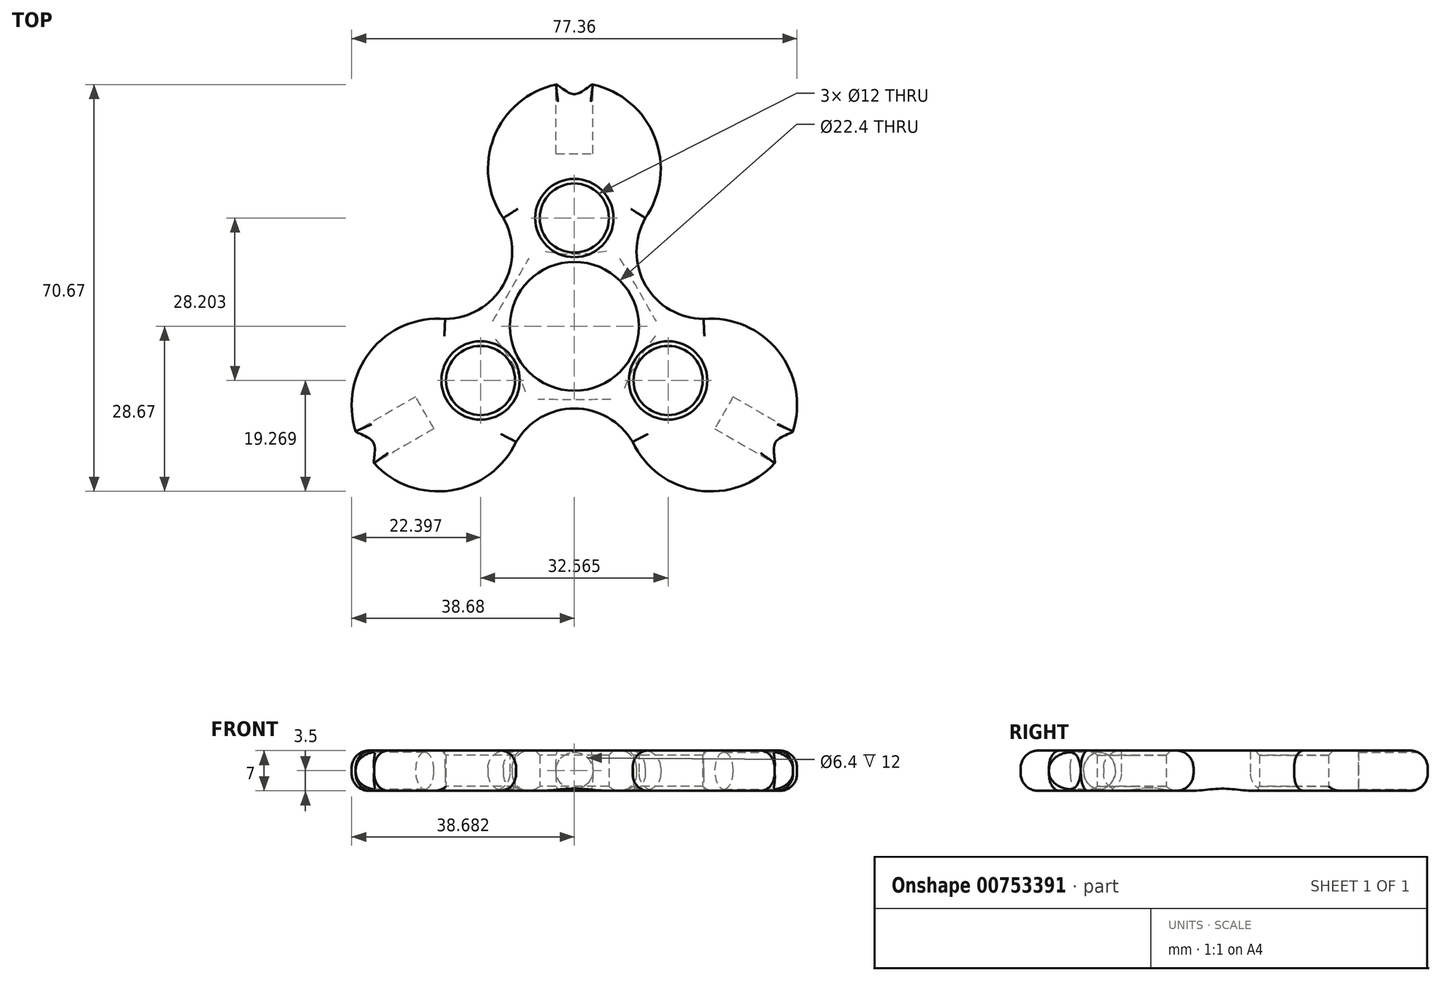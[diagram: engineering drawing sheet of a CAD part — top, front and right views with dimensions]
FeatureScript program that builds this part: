
annotation { "Feature Type Name" : "Feature", "Feature Type Description" : "" }
export const myFeature = defineFeature(function(context is Context, id is Id, definition is map)
    precondition{}
    {
        {
            var Q0;
            Q0=qCreatedBy(makeId("Top.planeOp"),FACE);
            var sketch = newSketch(context, id + "F0", { "sketchPlane" : qUnion([Q0])});
            skCircle(sketch, "E0", {"center": v(0, 0) * mm, "radius": 11.2 * mm});
            skLineSegment(sketch, "E1", {"start": v(0, 27.34) * mm, "end": v(0, -38.7) * mm, "construction": true});
            skArc(sketch, "E2", {"start": v(12.33, 18.8) * mm, "mid": v(13.96, 32.83) * mm, "end": v(3.2, 42) * mm});
            skPoint(sketch, "E3.startSnap0", {"position": v(0, 42.34) * mm});
            skArc(sketch, "E4", {"start": v(-3.2, 42) * mm, "mid": v(-13.96, 32.84) * mm, "end": v(-12.33, 18.8) * mm});
            skLineSegment(sketch, "E5", {"start": v(-3.2, 42) * mm, "end": v(-3.2, 42) * mm});
            skPoint(sketch, "E6.1.0", {"position": v(-36.67, -21.17) * mm});
            skArc(sketch, "E6.1.1", {"start": v(-34.77, -23.77) * mm, "mid": v(-21.46, -28.5) * mm, "end": v(-10.12, -20.08) * mm});
            skArc(sketch, "E6.1.3", {"start": v(-22.44, 1.28) * mm, "mid": v(-35.41, -4.33) * mm, "end": v(-37.97, -18.22) * mm});
            skPoint(sketch, "E6.2.0", {"position": v(36.67, -21.17) * mm});
            skArc(sketch, "E6.2.1", {"start": v(37.97, -18.23) * mm, "mid": v(35.42, -4.33) * mm, "end": v(22.45, 1.28) * mm});
            skArc(sketch, "E6.2.3", {"start": v(10.12, -20.07) * mm, "mid": v(21.45, -28.5) * mm, "end": v(34.77, -23.77) * mm});
            skArc(sketch, "E7", {"start": v(12.33, 18.8) * mm, "mid": v(12.37, 7.14) * mm, "end": v(22.45, 1.28) * mm});
            skArc(sketch, "E8.1.0", {"start": v(-22.44, 1.28) * mm, "mid": v(-12.37, 7.14) * mm, "end": v(-12.33, 18.8) * mm});
            skArc(sketch, "E8.2.0", {"start": v(10.12, -20.07) * mm, "mid": v(0, -14.28) * mm, "end": v(-10.12, -20.08) * mm});
            skCircle(sketch, "E9", {"center": v(0, 18.8) * mm, "radius": 6 * mm});
            skCircle(sketch, "E10.1.0", {"center": v(-16.28, -9.4) * mm, "radius": 6 * mm});
            skCircle(sketch, "E10.2.0", {"center": v(16.28, -9.4) * mm, "radius": 6 * mm});
            skLineSegment(sketch, "E11", {"start": v(34.77, -23.77) * mm, "end": v(37.97, -18.23) * mm});
            skLineSegment(sketch, "E12", {"start": v(-3.2, 42) * mm, "end": v(3.2, 42) * mm});
            skLineSegment(sketch, "E13", {"start": v(-37.97, -18.22) * mm, "end": v(-34.77, -23.77) * mm});
            skSolve(sketch);
        }
        {
            var Q0;
            Q0=makeQuery(id+"F0.imprint","IMPRINT",FACE,{"disambiguationData":[TD([[makeQuery(id+"F0.imprint","IMPRINT",EDGE,{"derivedFrom":sQuery(id+"F0.wireOp",EDGE,"E0")}),-1.0]])]});
            extrude(context, id + "F1", {"entities" : qUnion([Q0]), "depth" : 7 * mm, "offsetDistance" : 25 * mm});
        }
        {
            var Q0;
            Q0=makeQuery(id+"F1.opExtrude","CAP_EDGE",EDGE,{"disambiguationData":[OSD([sQuery(id+"F0.wireOp",EDGE,"E10.1.0")])],"isStart":false});
            var Q1;
            Q1=makeQuery(id+"F1.opExtrude","CAP_EDGE",EDGE,{"disambiguationData":[OSD([sQuery(id+"F0.wireOp",EDGE,"E9")])],"isStart":false});
            var Q2;
            Q2=makeQuery(id+"F1.opExtrude","CAP_EDGE",EDGE,{"disambiguationData":[OSD([sQuery(id+"F0.wireOp",EDGE,"E10.2.0")])],"isStart":false});
            var Q3;
            Q3=makeQuery(id+"F1.opExtrude","CAP_EDGE",EDGE,{"disambiguationData":[OSD([sQuery(id+"F0.wireOp",EDGE,"E10.2.0")])],"isStart":true});
            var Q4;
            Q4=makeQuery(id+"F1.opExtrude","CAP_EDGE",EDGE,{"disambiguationData":[OSD([sQuery(id+"F0.wireOp",EDGE,"E10.1.0")])],"isStart":true});
            var Q5;
            Q5=makeQuery(id+"F1.opExtrude","CAP_EDGE",EDGE,{"disambiguationData":[OSD([sQuery(id+"F0.wireOp",EDGE,"E9")])],"isStart":true});
            chamfer(context, id + "F2", {"entities" : qUnion([Q0, Q1, Q2, Q3, Q4, Q5]), "width" : 0.8 * mm, "tangentPropagation" : true});
        }
        {
            var Q0;
            Q0=makeQuery(id+"F1.opExtrude","SWEPT_FACE",FACE,{"disambiguationData":[OSD([sQuery(id+"F0.wireOp",EDGE,"E13")])]});
            var sketch = newSketch(context, id + "F3", { "sketchPlane" : qUnion([Q0])});
            skLineSegment(sketch, "E14", {"start": v(-3.2, 7) * mm, "end": v(3.2, 0) * mm, "construction": true});
            skLineSegment(sketch, "E15", {"start": v(-3.2, 0) * mm, "end": v(3.2, 7) * mm, "construction": true});
            skPoint(sketch, "E16", {"position": v(0, 3.5) * mm});
            skCircle(sketch, "E17", {"center": v(0, 3.5) * mm, "radius": 3.2 * mm});
            skSolve(sketch);
        }
        {
            var Q0;
            {var subQ0=sQuery(id+"F3.wireOp",EDGE,"E17");var subQ1=sQuery(id+"F0.wireOp",EDGE,"E13");var subQ2=makeQuery(id+"F3.imprint","INTERSECT",VERTEX,{"derivedFrom":[makeQuery(id+"F1.opExtrude","SWEPT_EDGE",EDGE,{"disambiguationData":[OSD([sQuery(id+"F0.wireOp",EDGE,"E6.1.1"),subQ1])]}),subQ0]});Q0=makeQuery(id+"F3.imprint","IMPRINT",FACE,{"disambiguationData":[TD([[makeQuery(id+"F3.imprint","IMPRINT",EDGE,{"disambiguationData":[TD([[subQ2,-1.0]])],"derivedFrom":subQ0}),1.0]])]});}
            extrude(context, id + "F4", {"entities" : qUnion([Q0]), "operationType" : NewBodyOperationType.REMOVE, "oppositeDirection" : true, "depth" : 12 * mm, "offsetDistance" : 25 * mm});
        }
        {
            var Q0;
            Q0=makeQuery(id+"F1.opExtrude","SWEPT_FACE",FACE,{"disambiguationData":[OSD([sQuery(id+"F0.wireOp",EDGE,"E11")])]});
            var sketch = newSketch(context, id + "F5", { "sketchPlane" : qUnion([Q0])});
            skLineSegment(sketch, "E18", {"start": v(-3.2, 7) * mm, "end": v(3.2, 0) * mm, "construction": true});
            skLineSegment(sketch, "E19", {"start": v(3.2, 7) * mm, "end": v(-3.2, 0) * mm, "construction": true});
            skCircle(sketch, "E20", {"center": v(0, 3.5) * mm, "radius": 3.2 * mm});
            skSolve(sketch);
        }
        {
            var Q0;
            {var subQ0=sQuery(id+"F5.wireOp",EDGE,"E20");var subQ1=sQuery(id+"F0.wireOp",EDGE,"E11");var subQ2=makeQuery(id+"F5.imprint","INTERSECT",VERTEX,{"derivedFrom":[makeQuery(id+"F1.opExtrude","SWEPT_EDGE",EDGE,{"disambiguationData":[OSD([sQuery(id+"F0.wireOp",EDGE,"E6.2.1"),subQ1])]}),subQ0]});Q0=makeQuery(id+"F5.imprint","IMPRINT",FACE,{"disambiguationData":[TD([[makeQuery(id+"F5.imprint","IMPRINT",EDGE,{"disambiguationData":[TD([[subQ2,-1.0]])],"derivedFrom":subQ0}),1.0]])]});}
            extrude(context, id + "F6", {"entities" : qUnion([Q0]), "operationType" : NewBodyOperationType.REMOVE, "oppositeDirection" : true, "depth" : 12 * mm, "offsetDistance" : 25 * mm});
        }
        {
            var Q0;
            Q0=makeQuery(id+"F1.opExtrude","SWEPT_FACE",FACE,{"disambiguationData":[OSD([sQuery(id+"F0.wireOp",EDGE,"E12")])]});
            var sketch = newSketch(context, id + "F7", { "sketchPlane" : qUnion([Q0])});
            skLineSegment(sketch, "E21", {"start": v(-3.2, 7) * mm, "end": v(3.2, 0) * mm, "construction": true});
            skCircle(sketch, "E22", {"center": v(0, 3.5) * mm, "radius": 3.2 * mm});
            skSolve(sketch);
        }
        {
            var Q0;
            {var subQ0=sQuery(id+"F7.wireOp",EDGE,"E22");var subQ1=sQuery(id+"F0.wireOp",EDGE,"E12");var subQ2=makeQuery(id+"F7.imprint","INTERSECT",VERTEX,{"derivedFrom":[makeQuery(id+"F1.opExtrude","SWEPT_EDGE",EDGE,{"disambiguationData":[OSD([sQuery(id+"F0.wireOp",EDGE,"E2"),subQ1])]}),subQ0]});Q0=makeQuery(id+"F7.imprint","IMPRINT",FACE,{"disambiguationData":[TD([[makeQuery(id+"F7.imprint","IMPRINT",EDGE,{"disambiguationData":[TD([[subQ2,1.0]])],"derivedFrom":subQ0}),1.0]])]});}
            extrude(context, id + "F8", {"entities" : qUnion([Q0]), "operationType" : NewBodyOperationType.REMOVE, "oppositeDirection" : true, "depth" : 12 * mm, "offsetDistance" : 25 * mm});
        }
        {
            var Q0;
            Q0=makeQuery(id+"F1.opExtrude","CAP_EDGE",EDGE,{"disambiguationData":[OSD([sQuery(id+"F0.wireOp",EDGE,"E6.2.3")])],"isStart":false});
            var Q1;
            Q1=makeQuery(id+"F1.opExtrude","CAP_EDGE",EDGE,{"disambiguationData":[OSD([sQuery(id+"F0.wireOp",EDGE,"E8.2.0")])],"isStart":false});
            var Q2;
            Q2=makeQuery(id+"F1.opExtrude","CAP_EDGE",EDGE,{"disambiguationData":[OSD([sQuery(id+"F0.wireOp",EDGE,"E6.1.1")])],"isStart":false});
            var Q3;
            Q3=makeQuery(id+"F1.opExtrude","CAP_EDGE",EDGE,{"disambiguationData":[OSD([sQuery(id+"F0.wireOp",EDGE,"E6.1.3")])],"isStart":false});
            var Q4;
            Q4=makeQuery(id+"F1.opExtrude","CAP_EDGE",EDGE,{"disambiguationData":[OSD([sQuery(id+"F0.wireOp",EDGE,"E8.1.0")])],"isStart":false});
            var Q5;
            Q5=makeQuery(id+"F1.opExtrude","CAP_EDGE",EDGE,{"disambiguationData":[OSD([sQuery(id+"F0.wireOp",EDGE,"E4")])],"isStart":false});
            var Q6;
            Q6=makeQuery(id+"F1.opExtrude","CAP_EDGE",EDGE,{"disambiguationData":[OSD([sQuery(id+"F0.wireOp",EDGE,"E2")])],"isStart":false});
            var Q7;
            Q7=makeQuery(id+"F1.opExtrude","CAP_EDGE",EDGE,{"disambiguationData":[OSD([sQuery(id+"F0.wireOp",EDGE,"E7")])],"isStart":false});
            var Q8;
            Q8=makeQuery(id+"F1.opExtrude","CAP_EDGE",EDGE,{"disambiguationData":[OSD([sQuery(id+"F0.wireOp",EDGE,"E6.2.1")])],"isStart":false});
            var Q9;
            Q9=makeQuery(id+"F1.opExtrude","CAP_EDGE",EDGE,{"disambiguationData":[OSD([sQuery(id+"F0.wireOp",EDGE,"E11")])],"isStart":false});
            var Q10;
            Q10=makeQuery(id+"F1.opExtrude","CAP_EDGE",EDGE,{"disambiguationData":[OSD([sQuery(id+"F0.wireOp",EDGE,"E13")])],"isStart":false});
            var Q11;
            Q11=makeQuery(id+"F1.opExtrude","CAP_EDGE",EDGE,{"disambiguationData":[OSD([sQuery(id+"F0.wireOp",EDGE,"E12")])],"isStart":false});
            var Q12;
            Q12=makeQuery(id+"F1.opExtrude","CAP_EDGE",EDGE,{"disambiguationData":[OSD([sQuery(id+"F0.wireOp",EDGE,"E6.2.1")])],"isStart":true});
            var Q13;
            Q13=makeQuery(id+"F1.opExtrude","CAP_EDGE",EDGE,{"disambiguationData":[OSD([sQuery(id+"F0.wireOp",EDGE,"E7")])],"isStart":true});
            var Q14;
            Q14=makeQuery(id+"F1.opExtrude","CAP_EDGE",EDGE,{"disambiguationData":[OSD([sQuery(id+"F0.wireOp",EDGE,"E2")])],"isStart":true});
            var Q15;
            Q15=makeQuery(id+"F1.opExtrude","CAP_EDGE",EDGE,{"disambiguationData":[OSD([sQuery(id+"F0.wireOp",EDGE,"E12")])],"isStart":true});
            var Q16;
            Q16=makeQuery(id+"F1.opExtrude","CAP_EDGE",EDGE,{"disambiguationData":[OSD([sQuery(id+"F0.wireOp",EDGE,"E4")])],"isStart":true});
            var Q17;
            Q17=makeQuery(id+"F1.opExtrude","CAP_EDGE",EDGE,{"disambiguationData":[OSD([sQuery(id+"F0.wireOp",EDGE,"E8.1.0")])],"isStart":true});
            var Q18;
            Q18=makeQuery(id+"F1.opExtrude","CAP_EDGE",EDGE,{"disambiguationData":[OSD([sQuery(id+"F0.wireOp",EDGE,"E6.1.3")])],"isStart":true});
            var Q19;
            Q19=makeQuery(id+"F1.opExtrude","CAP_EDGE",EDGE,{"disambiguationData":[OSD([sQuery(id+"F0.wireOp",EDGE,"E13")])],"isStart":true});
            var Q20;
            Q20=makeQuery(id+"F1.opExtrude","CAP_FACE",FACE,{"disambiguationData":[OSD([sQuery(id+"F0.wireOp",EDGE,"E0"),sQuery(id+"F0.wireOp",EDGE,"E2"),sQuery(id+"F0.wireOp",EDGE,"E4"),sQuery(id+"F0.wireOp",EDGE,"E6.1.1"),sQuery(id+"F0.wireOp",EDGE,"E6.1.3"),sQuery(id+"F0.wireOp",EDGE,"E6.2.1"),sQuery(id+"F0.wireOp",EDGE,"E6.2.3"),sQuery(id+"F0.wireOp",EDGE,"E7"),sQuery(id+"F0.wireOp",EDGE,"E8.1.0"),sQuery(id+"F0.wireOp",EDGE,"E8.2.0"),sQuery(id+"F0.wireOp",EDGE,"E9"),sQuery(id+"F0.wireOp",EDGE,"E10.1.0"),sQuery(id+"F0.wireOp",EDGE,"E10.2.0"),sQuery(id+"F0.wireOp",EDGE,"E11"),sQuery(id+"F0.wireOp",EDGE,"E12"),sQuery(id+"F0.wireOp",EDGE,"E13")])],"isStart":true});
            var Q21;
            Q21=makeQuery(id+"F1.opExtrude","CAP_EDGE",EDGE,{"disambiguationData":[OSD([sQuery(id+"F0.wireOp",EDGE,"E8.2.0")])],"isStart":true});
            var Q22;
            Q22=makeQuery(id+"F1.opExtrude","CAP_EDGE",EDGE,{"disambiguationData":[OSD([sQuery(id+"F0.wireOp",EDGE,"E6.2.3")])],"isStart":true});
            var Q23;
            Q23=makeQuery(id+"F1.opExtrude","CAP_EDGE",EDGE,{"disambiguationData":[OSD([sQuery(id+"F0.wireOp",EDGE,"E11")])],"isStart":true});
            fillet(context, id + "F9", {"entities" : qUnion([Q0, Q1, Q2, Q3, Q4, Q5, Q6, Q7, Q8, Q9, Q10, Q11, Q12, Q13, Q14, Q15, Q16, Q17, Q18, Q19, Q20, Q21, Q22, Q23]), "radius" : 3 * mm, "tangentPropagation" : true, "allowEdgeOverflow" : false});
        }
    });
